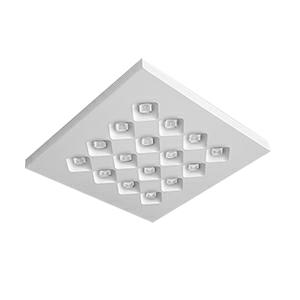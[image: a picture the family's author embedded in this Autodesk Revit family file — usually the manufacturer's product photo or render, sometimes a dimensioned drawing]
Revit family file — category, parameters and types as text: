
# Revit family: 3f_filippi_-_3f_diagon_3f_filippi_-_23102_a0686_-_3f_diagon_25w-930_dali_596x596___corn_plaf__7bcb
name_source: partatom
category: Lighting Fixtures
units: mm (PartAtom-declared; Revit-internal decimal feet)

## family parameters
Cut with Voids When Loaded = No
Host = Face
Light Source = No
Part Type = Normal
Room Calculation Point = No
Round Connector Dimension = Use Diameter
Shared = No

## types (1)
- 3F Filippi - 3F Dìagon (1 x LED, 3103 lm, 28 W, 3000 K)
    Apparent Load = 28 VA
    Approval mark = CE
    CIE Flux Codes = 67 96 100 100 100
    Color Rendering = 90
    Color Temperature = 3000 K
    Control Gear = Electronic transformer
    Default Elevation = 1800 mm
    Description = ILLUMINOTECHNICAL
Luminous efficiency 100% (DLOR 100%, ULOR 0%).
Initial luminous flux of the luminaire 3103 lm.
Direct symmetric distribution.
Installation Interdistance Transv.D = 1.39 x hu - Long.D = 1.39 x hu.
Average luminance <1500 cd/m² for radial angles >65°.
Tabular UGR (CIE 117 - 4H-8H; S=0.25H; 70/50/20): RUG 16.3 - 16.2.
Beam angle: 93° - 92°.
Luminous efficacy 111 lm/W.
Lifetime (L95/B10): 30000 h. (tq+25°C)
Lifetime (L90/B10): 50000 h. (tq+25°C)
Lifetime (L80/B10): 80000 h. (tq+25°C)
Lifetime (L75/B10): 100000 h. (tq+25°C)
Sudden decreased luminous flux after 50000 hours: 0% (C0).
Photobiological safety in compliance with IEC/TR 62778: RG0 risk exempt, (IEC 62471).
In compliance with IEC/EN 62722-2-1 - IEC/EN 62717 standards.

SOURCE
Squared LED module 25W/930.
Energy efficiency class (UE 2019/2020 - UE 2019/2015): E.
CIE 13.3 Colour rendering index: CRI >90 (R9 >50%).
IES TM-30 Fidelity Index: Rf = 92 Rg = 101.
CCT nominal colour temperature 3000 K.
Colour initial tolerance (MacAdam): SDCM 3.

MECHANICAL
Housing in hot-galvanised steel, painted in white polyester.
Honeycombed diagonal screen in white anti-glare polycarbonate.
Rhomboidal lenses with differentiated surfaces, etched and prismatic to optimise the orientation of the luminous flux, in transparent methacrylate (PMMA).
Luminaire with limited surface temperature. - D - (EN 60598-2-24)
Dimensions: 600x600 mm, height 40 mm. Weight 6.095 kg.
IP43 protection degree for exposed part, IP20 for recessed part.
Mechanical strength to impacts IK06 (1 joule).
Glow-wire test resistance 650°C.

ELECTRICAL
Halogen Free DALI-2, PUSH-DIM, electronic wiring 230V-50/60Hz, power factor 0.95 at full load, THD <25%, constant output current, class I, 1 driver, 1 DALI addresse.
Power of the luminaire 28 W.
ENEC - CE.
SAFE FLICKER: PstLM=<1 and SVM=<0.4 (IEC TR 61547-1 and IEC TR 63158), to ensure a more comfortable and safe light.
Luminaire compliant with EN 60598-2-22 for power supply from a centralised emergency system CPSS (Central Power Supply System), not incorporated in the luminaire - high risk areas excluded. The default power and flux are 100% in AC and 15% in DC.
Ambient temperature from 0°C to +25°C.
Temperature class T6 max 85°C.
Quick connection.
Relative humidity UR: <85%.

INSTALLATION
Ceiling.
Height only 40 mm.
All accessories dedicated to this product are available on the Catalog and on our website www.3F-Filippi.com.

ACCESSORIES
A0686 - 596x596 Diagon frame for Ceiling installation.

APPLICATIONS
Environments: staterooms, with VDTs, offices.
Environments with exacting visual tasks, where diffused soft light for optimum visual comfort is required.

LIGHT MANAGEMENT
Recommended minimum setting: 10%.
The device, equipped with DALI-2 driver, can be controlled manually with 3F Easy Dim technology or automatically/manually with 3F Smart Dimming technology and/or centralised DALI systems.
DALI-2 certification guarantees interoperability with other devices with the same certification.
In electrical systems without a regulation system (manual or automatic) and DALI bus, a suitable jumper must be made on the DA-DA terminals of the appliance.

WARNING
Luminaire designed for disposal/recycling at end-of-life.
Replaceable (LED only) light source by a professional. Replaceable control gear by a professional.
    Height = 0 mm  [stored 0 ft]
    Lamp = 1 x LED
    Lamp Light Flux = 3103 lm
    Lamp Power = 28 W
    Lamp count = 1
    Length = 600 mm
    Lifetime = 50000 h
    Luminous efficacy = 111 lm/W
    Manufacturer = 3F Filippi
    ModVariant = No
    Model = 3F Filippi - 23102+A0686 - 3F Diagon 25W-930 DALI 596x596 + Corn.plaf.
    Mounting Place = Ceiling
    Mounting Type = Recessed
    Number of Poles = 1
    OnlyDefault = Yes
    Power Factor = 1
    Product Name = 3F Filippi - 3F Dìagon
    Product group = recessed luminaire
    ProductGroupID = 4
    Protection Class = Protection class I
    Protection Degree = IP 20
    RLX_Detail_Level = 1
    RLX_Emergency_Light_Flux = 0 lm
    RLX_Emergency_Type = 0
    RLX_Emergency_Type_DB = No
    RlxData = <blob elided: 97905 chars, md5=fc71d5bf>
    Socket = socket
    Standby Power = 0 W
    System Light Flux = 3103 lm
    System Power = 28 W
    Type Comments = Product without accessories
    Type Image = 3ffilippi_3f_diagon__a0686.jpg
    URL = http://relux.com
    VarID = ---
    Voltage = 0 V
    Weight = 0.00 kg
    Width = 600 mm

note: [stored X ft] marks values corroborated as IEEE doubles in the binary element streams (Revit-internal decimal feet)

## geometry (parser evidence)
native form markers: Blend x4, Sweep x10
no freeform markers — native parametric forms only
